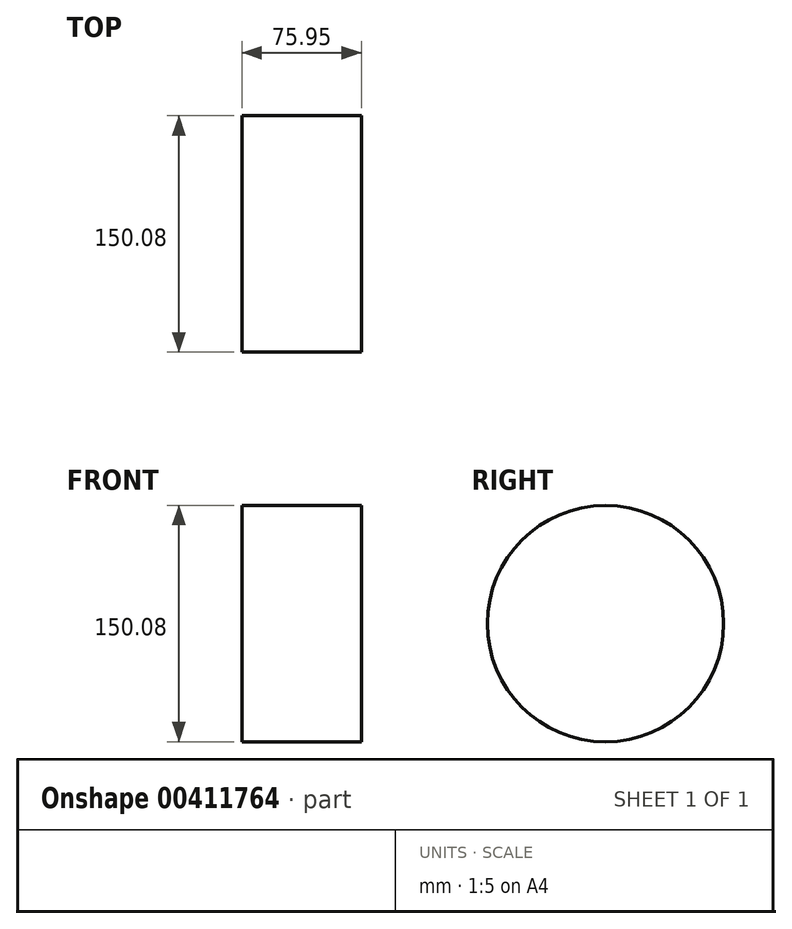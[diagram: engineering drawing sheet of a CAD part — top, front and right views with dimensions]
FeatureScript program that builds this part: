
annotation { "Feature Type Name" : "Feature", "Feature Type Description" : "" }
export const myFeature = defineFeature(function(context is Context, id is Id, definition is map)
    precondition{}
    {
        {
            var Q0;
            Q0=qCreatedBy(makeId("Right.planeOp"),FACE);
            var sketch = newSketch(context, id + "F0", { "sketchPlane" : qUnion([Q0])});
            skCircle(sketch, "E0", {"center": v(0, 0) * mm, "radius": 75.04 * mm});
            skSolve(sketch);
        }
        {
            var Q0;
            Q0=makeQuery(id+"F0.imprint","IMPRINT",FACE,{"disambiguationData":[TD([[makeQuery(id+"F0.imprint","IMPRINT",EDGE,{"derivedFrom":sQuery(id+"F0.wireOp",EDGE,"E0")}),1.0]])]});
            var Q1;
            Q1 = qSketchRegion(id + "F0", true);
            extrude(context, id + "F1", {"entities" : qUnion([Q0, Q1]), "depth" : 75.95 * mm});
        }
    });
